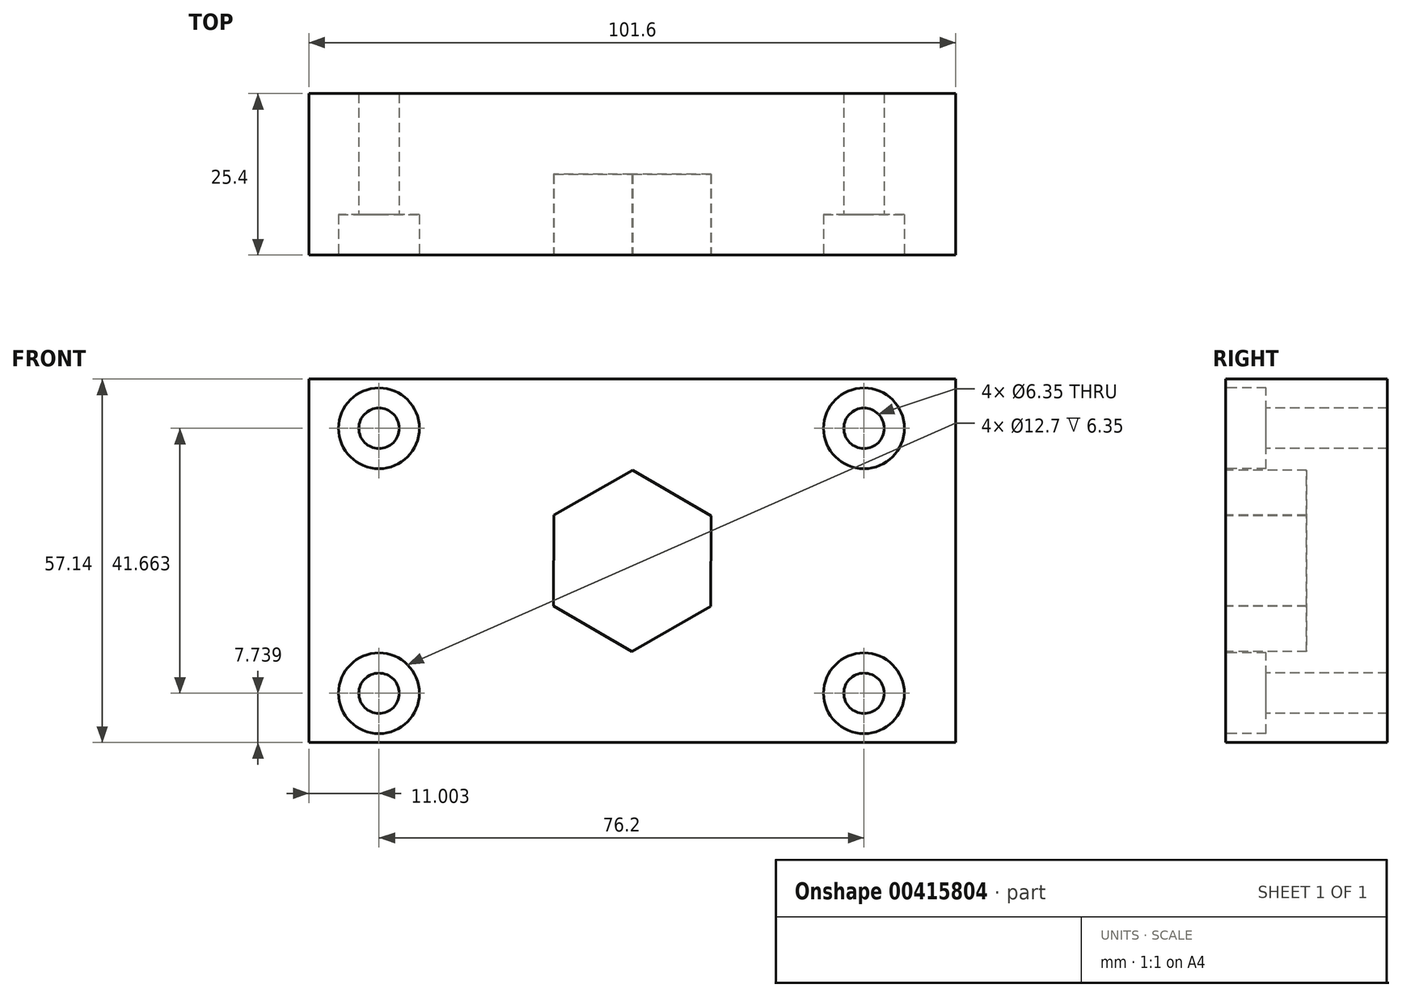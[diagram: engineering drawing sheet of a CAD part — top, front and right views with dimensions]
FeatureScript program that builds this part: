
annotation { "Feature Type Name" : "Feature", "Feature Type Description" : "" }
export const myFeature = defineFeature(function(context is Context, id is Id, definition is map)
    precondition{}
    {
        {
            var Q0;
            Q0=qCreatedBy(makeId("Front.planeOp"),FACE);
            var sketch = newSketch(context, id + "F0", { "sketchPlane" : qUnion([Q0])});
            skLineSegment(sketch, "E0.bottom", {"start": v(50.8, -28.58) * mm, "end": v(-50.8, -28.58) * mm});
            skLineSegment(sketch, "E0.top", {"start": v(50.8, 28.58) * mm, "end": v(-50.8, 28.58) * mm});
            skLineSegment(sketch, "E0.left", {"start": v(50.8, -28.58) * mm, "end": v(50.8, 28.58) * mm});
            skLineSegment(sketch, "E0.right", {"start": v(-50.8, -28.58) * mm, "end": v(-50.8, 28.58) * mm});
            skPoint(sketch, "E0.middle", {"position": v(0, 0) * mm});
            skSolve(sketch);
        }
        {
            var Q0;
            Q0 = qSketchRegion(id + "F0", true);
            extrude(context, id + "F1", {"entities" : qUnion([Q0]), "depth" : 25.4 * mm});
        }
        {
            var Q0;
            Q0=makeQuery(id+"F1.opExtrude","CAP_FACE",FACE,{"disambiguationData":[OSD([sQuery(id+"F0.wireOp",EDGE,"E0.bottom"),sQuery(id+"F0.wireOp",EDGE,"E0.top"),sQuery(id+"F0.wireOp",EDGE,"E0.left"),sQuery(id+"F0.wireOp",EDGE,"E0.right")])],"isStart":false});
            var sketch = newSketch(context, id + "F2", { "sketchPlane" : qUnion([Q0])});
            skCircle(sketch, "E1", {"center": v(-39.8, 20.83) * mm, "radius": 3.41 * mm});
            skCircle(sketch, "E2.1.0.0", {"center": v(36.4, 20.83) * mm, "radius": 3.41 * mm});
            skLineSegment(sketch, "E2.direction1", {"start": v(-39.8, 20.83) * mm, "end": v(36.4, 20.83) * mm, "construction": true});
            skLineSegment(sketch, "E3", {"start": v(-50.8, 0) * mm, "end": v(50.8, 0) * mm});
            skCircle(sketch, "E4.MirrorC", {"center": v(36.4, -20.83) * mm, "radius": 3.41 * mm});
            skCircle(sketch, "E5.MirrorC", {"center": v(-39.8, -20.83) * mm, "radius": 3.41 * mm});
            skText(sketch, "E6", { "text": " COAST CUSTOM ENGRAVING", "fontName": "Arimo-Bold.ttf"});
            const initialGuessF2  = {"E6": [-0.04857, -0.00475, 1, 0, 0.00475]};
            skSetInitialGuess(sketch, initialGuessF2);
            skSolve(sketch);
        }
        {
            var Q0;
            Q0=sQuery(id+"F2.wireOp",VERTEX,"E2.direction1.end");
            var Q1;
            Q1=sQuery(id+"F2.wireOp",VERTEX,"E4.MirrorC.center");
            var Q2;
            Q2=sQuery(id+"F2.wireOp",VERTEX,"E2.direction1.start");
            var Q3;
            Q3=sQuery(id+"F2.wireOp",VERTEX,"E5.MirrorC.center");
            var Q4;
            Q4=makeQuery(id+"F1.opExtrude","SWEPT_BODY",BODY,{"disambiguationData":[OSD([sQuery(id+"F0.wireOp",EDGE,"E0.bottom"),sQuery(id+"F0.wireOp",EDGE,"E0.top"),sQuery(id+"F0.wireOp",EDGE,"E0.left"),sQuery(id+"F0.wireOp",EDGE,"E0.right")])]});
            hole(context, id + "F3", {"style" : HoleStyle.C_BORE, "endStyle" : HoleEndStyle.THROUGH, "holeDiameter" : 6.35 * mm, "cBoreDiameter" : 12.7 * mm, "cBoreDepth" : 6.35 * mm, "isTappedThrough" : true, "tappedDepth" : 12.7 * mm, "tapClearance" : 3, "locations" : qUnion([Q0, Q1, Q2, Q3]), "scope" : qUnion([Q4])});
        }
        {
            var Q0;
            Q0=makeQuery(id+"F1.opExtrude","CAP_FACE",FACE,{"disambiguationData":[OSD([sQuery(id+"F0.wireOp",EDGE,"E0.bottom"),sQuery(id+"F0.wireOp",EDGE,"E0.top"),sQuery(id+"F0.wireOp",EDGE,"E0.left"),sQuery(id+"F0.wireOp",EDGE,"E0.right")])],"isStart":false});
            var sketch = newSketch(context, id + "F4", { "sketchPlane" : qUnion([Q0])});
            skCircle(sketch, "E7.cCircle", {"center": v(0, 0) * mm, "radius": 12.35 * mm, "construction": true});
            skLineSegment(sketch, "E7.0", {"start": v(12.32, -7.16) * mm, "end": v(-0.04, -14.25) * mm});
            skLineSegment(sketch, "E7.1", {"start": v(-0.04, -14.25) * mm, "end": v(-12.37, -7.1) * mm});
            skLineSegment(sketch, "E7.2", {"start": v(-12.37, -7.1) * mm, "end": v(-12.32, 7.16) * mm});
            skLineSegment(sketch, "E7.3", {"start": v(-12.32, 7.16) * mm, "end": v(0.04, 14.25) * mm});
            skLineSegment(sketch, "E7.4", {"start": v(0.04, 14.25) * mm, "end": v(12.37, 7.1) * mm});
            skLineSegment(sketch, "E7.5", {"start": v(12.37, 7.1) * mm, "end": v(12.32, -7.16) * mm});
            skPoint(sketch, "E7.0.midPoint", {"position": v(6.14, -10.7) * mm});
            skSolve(sketch);
        }
        {
            var Q0;
            Q0=makeQuery(id+"F4.imprint","IMPRINT",FACE,{"disambiguationData":[TD([[makeQuery(id+"F4.imprint","IMPRINT",EDGE,{"derivedFrom":sQuery(id+"F4.wireOp",EDGE,"E7.0")}),-1.0]])]});
            extrude(context, id + "F5", {"entities" : qUnion([Q0]), "operationType" : NewBodyOperationType.REMOVE, "oppositeDirection" : true, "depth" : 12.7 * mm});
        }
    });
